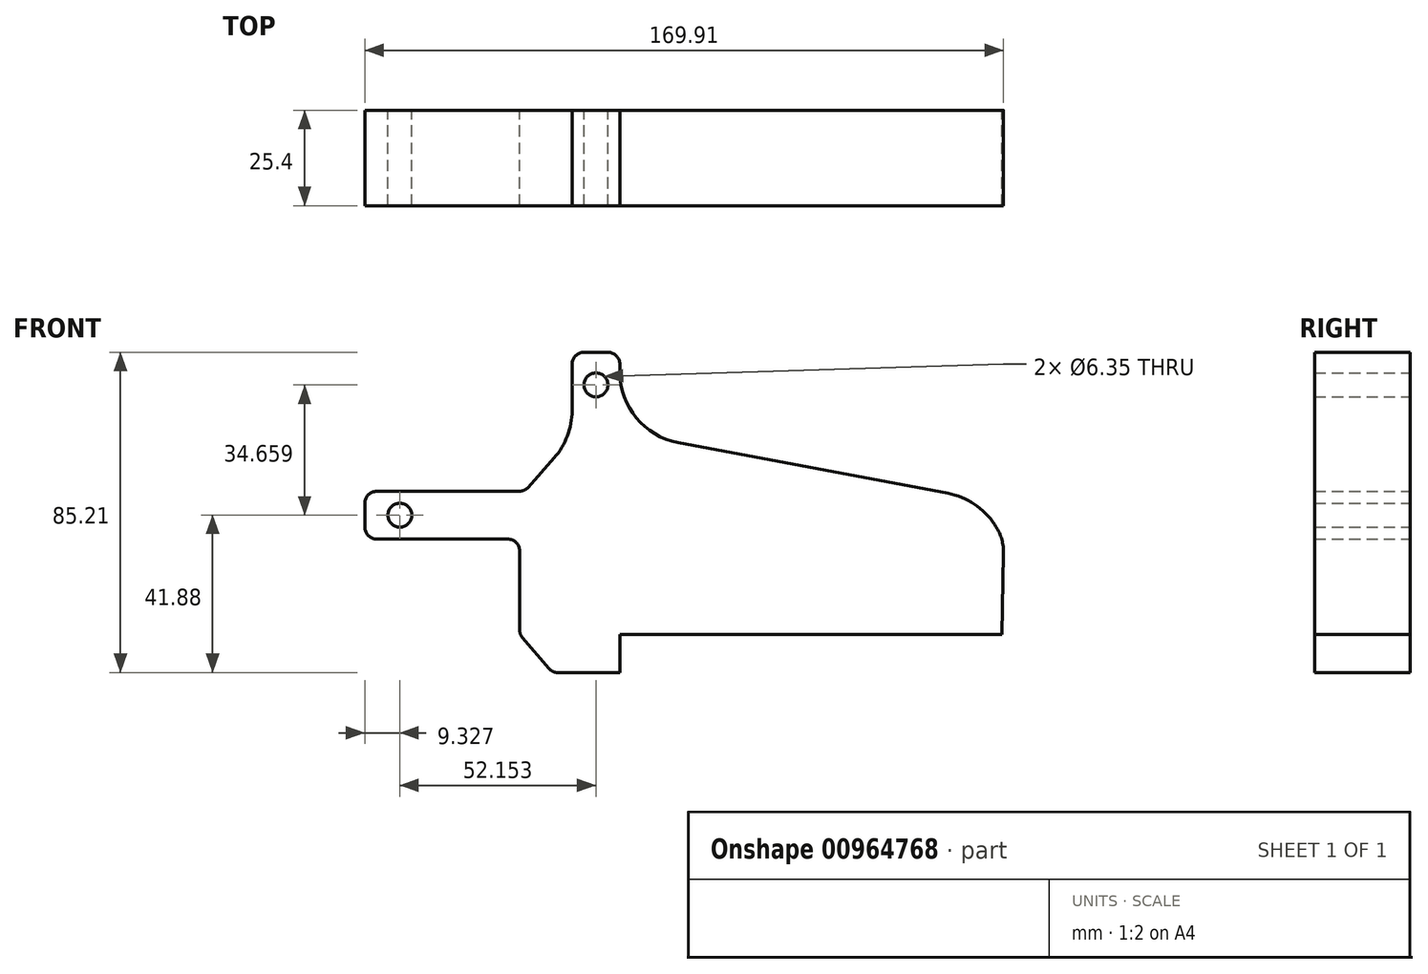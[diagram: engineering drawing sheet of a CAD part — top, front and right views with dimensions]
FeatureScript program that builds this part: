
annotation { "Feature Type Name" : "Feature", "Feature Type Description" : "" }
export const myFeature = defineFeature(function(context is Context, id is Id, definition is map)
    precondition{}
    {
        {
            var Q0;
            Q0=qCreatedBy(makeId("Front.planeOp"),FACE);
            var sketch = newSketch(context, id + "F0", { "sketchPlane" : qUnion([Q0])});
            skLineSegment(sketch, "E0", {"start": v(0, 0) * mm, "end": v(101.6, 0.04) * mm});
            skLineSegment(sketch, "E1", {"start": v(101.6, 0.04) * mm, "end": v(102.08, 21.51) * mm});
            skLineSegment(sketch, "E2", {"start": v(100.02, 28.72) * mm, "end": v(99.68, 29.26) * mm});
            skLineSegment(sketch, "E3", {"start": v(87.23, 37.58) * mm, "end": v(15.53, 51.07) * mm});
            skLineSegment(sketch, "E4", {"start": v(0, 69.8) * mm, "end": v(0, 71.9) * mm});
            skLineSegment(sketch, "E5", {"start": v(-3.18, 75.08) * mm, "end": v(-9.53, 75.08) * mm});
            skLineSegment(sketch, "E6", {"start": v(-12.7, 71.9) * mm, "end": v(-12.7, 59.59) * mm});
            skLineSegment(sketch, "E7", {"start": v(-17.48, 46.96) * mm, "end": v(-24.37, 39.17) * mm});
            skLineSegment(sketch, "E8", {"start": v(-26.75, 38.1) * mm, "end": v(-64.66, 38.1) * mm});
            skLineSegment(sketch, "E9", {"start": v(-67.83, 34.93) * mm, "end": v(-67.83, 28.57) * mm});
            skLineSegment(sketch, "E10", {"start": v(-64.66, 25.4) * mm, "end": v(-29.82, 25.4) * mm});
            skLineSegment(sketch, "E11", {"start": v(-26.64, 22.23) * mm, "end": v(-26.64, 1.18) * mm});
            skLineSegment(sketch, "E12", {"start": v(-25.87, -0.9) * mm, "end": v(-18.84, -9.03) * mm});
            skLineSegment(sketch, "E13", {"start": v(0, -10.13) * mm, "end": v(-16.44, -10.13) * mm});
            skLineSegment(sketch, "E14", {"start": v(0, -10.13) * mm, "end": v(0, 0) * mm});
            skPoint(sketch, "E15.visualSharp", {"position": v(102.16, 25.44) * mm});
            skArc(sketch, "E15.filletArc", {"start": v(102.08, 21.51) * mm, "mid": v(101.6, 25.27) * mm, "end": v(100.02, 28.72) * mm});
            skPoint(sketch, "E16.visualSharp", {"position": v(95.23, 36.08) * mm});
            skArc(sketch, "E16.filletArc", {"start": v(99.68, 29.26) * mm, "mid": v(94.3, 34.7) * mm, "end": v(87.23, 37.58) * mm});
            skPoint(sketch, "E17.visualSharp", {"position": v(0, 53.99) * mm});
            skArc(sketch, "E17.filletArc", {"start": v(0, 69.8) * mm, "mid": v(4.39, 57.63) * mm, "end": v(15.53, 51.07) * mm});
            skPoint(sketch, "E18.visualSharp", {"position": v(-12.7, 52.37) * mm});
            skArc(sketch, "E18.filletArc", {"start": v(-17.48, 46.96) * mm, "mid": v(-13.94, 52.84) * mm, "end": v(-12.7, 59.59) * mm});
            skPoint(sketch, "E19.visualSharp", {"position": v(-12.7, 75.08) * mm});
            skArc(sketch, "E19.filletArc", {"start": v(-9.53, 75.08) * mm, "mid": v(-11.77, 74.15) * mm, "end": v(-12.7, 71.9) * mm});
            skPoint(sketch, "E20.visualSharp", {"position": v(0, 75.08) * mm});
            skArc(sketch, "E20.filletArc", {"start": v(0, 71.9) * mm, "mid": v(-0.93, 74.15) * mm, "end": v(-3.18, 75.08) * mm});
            skPoint(sketch, "E21.visualSharp", {"position": v(-67.83, 25.4) * mm});
            skArc(sketch, "E21.filletArc", {"start": v(-67.83, 28.57) * mm, "mid": v(-66.9, 26.33) * mm, "end": v(-64.66, 25.4) * mm});
            skPoint(sketch, "E22.visualSharp", {"position": v(-67.83, 38.1) * mm});
            skArc(sketch, "E22.filletArc", {"start": v(-64.66, 38.1) * mm, "mid": v(-66.9, 37.17) * mm, "end": v(-67.83, 34.93) * mm});
            skPoint(sketch, "E23.visualSharp", {"position": v(-26.64, 25.4) * mm});
            skArc(sketch, "E23.filletArc", {"start": v(-26.64, 22.23) * mm, "mid": v(-27.57, 24.47) * mm, "end": v(-29.82, 25.4) * mm});
            skPoint(sketch, "E24.visualSharp", {"position": v(-25.32, 38.1) * mm});
            skArc(sketch, "E24.filletArc", {"start": v(-26.75, 38.1) * mm, "mid": v(-25.45, 38.38) * mm, "end": v(-24.37, 39.17) * mm});
            skPoint(sketch, "E25.visualSharp", {"position": v(-26.64, 0) * mm});
            skArc(sketch, "E25.filletArc", {"start": v(-26.64, 1.18) * mm, "mid": v(-26.45, 0.07) * mm, "end": v(-25.87, -0.9) * mm});
            skPoint(sketch, "E26.visualSharp", {"position": v(-17.89, -10.13) * mm});
            skArc(sketch, "E26.filletArc", {"start": v(-18.84, -9.03) * mm, "mid": v(-17.76, -9.84) * mm, "end": v(-16.44, -10.13) * mm});
            skCircle(sketch, "E27", {"center": v(-58.5, 31.75) * mm, "radius": 3.18 * mm});
            skPoint(sketch, "E27.centerSnap0", {"position": v(-67.83, 31.75) * mm});
            skCircle(sketch, "E28", {"center": v(-6.35, 66.4) * mm, "radius": 3.18 * mm});
            skPoint(sketch, "E28.centerSnap0", {"position": v(-6.35, 75.08) * mm});
            skSolve(sketch);
        }
        {
            var Q0;
            Q0 = qSketchRegion(id + "F0", true);
            extrude(context, id + "F1", {"entities" : qUnion([Q0]), "depth" : 25.4 * mm, "offsetDistance" : 25.4 * mm});
        }
    });
